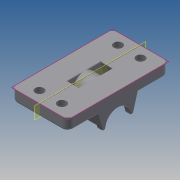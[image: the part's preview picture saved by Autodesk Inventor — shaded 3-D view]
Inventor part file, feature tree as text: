
AUTODESK INVENTOR PART (.ipt)
format: ipt  version: 2014 (Build 180170000, 170)  size: 468,480 bytes
history: native  units: in
note: dims shown in document units (in); Inventor stores cm internally (conversion verified against a paired STEP export)
features: fillet x9, extrude x7, sketch x7, plane x1, mirror x1
ambient origin geometry x8: Origin, YZ Plane, XZ Plane, XY Plane, X Axis, Y Axis, Z Axis, Center Point
bodies: Body1 (feature_tree)
feature tree (25):
  extrude  "Extrusion12"  Depth=1.0441in
  sketch  "Sketch13"  dims[d0=1.1713in d1=1.0441in]
  plane  "Work Plane2"
  extrude  "Extrusion14"  Depth=2.3622in
  extrude  "Extrusion15"  Depth=0.9843in
  mirror  "Mirror2"
  extrude  "Extrusion16"  Depth=0.9449in
  extrude  "Extrusion17"  Depth=0.2362in TaperAngle=0.0deg
  extrude  "Extrusion18"  Depth=0.3346in
  extrude  "Extrusion19"  Depth=0.0197in TaperAngle=0.0deg
  fillet  "Fillet11"  Radius=0.0591in
  fillet  "Fillet12"  Radius=0.1181in
  fillet  "Fillet13"  Radius=0.0394in
  fillet  "Fillet14"  Radius=0.1181in
  fillet  "Fillet15"  Radius=0.1575in
  fillet  "Fillet16"  Radius=0.1575in
  fillet  "Fillet17"  Radius=0.2362in
  fillet  "Fillet18"  Radius=0.4724in
  fillet  "Fillet19"  Radius=0.1811in
  sketch  "Sketch14"  dims[d2=1.5748in d5=2.3622in]
  sketch  "Sketch15"  dims[d6=0.1969in d7=0.9843in]
  sketch  "Sketch16"  dims[d64=0.3543in d65=0.9449in]
  sketch  "Sketch17"  dims[d66=1.7717in d70=0.2362in d71=0.0in]
  sketch  "Sketch18"  dims[d76=0.6299in d77=0.3346in]
  sketch  "Sketch19"  dims[d78=0.1181in d79=1.1811in d80=0.0in d81=0.0591in d82=0.1181in d83=0.0in d84=0.0394in d85=0.1181in d86=0.0in d87=0.1575in d88=0.1575in d89=0.2362in d90=0.0in d91=0.4724in d92=0.1811in d93=1.6535in d94=0.4724in d95=0.2362in d96=0.0in d106=0.0197in d107=0.0197in d108=0.0197in d109=0.0197in d110=0.0197in d111=1.1811in d112=2.126in d113=0.0in d114=0.1181in d115=0.0394in d116=0.2854in d117=0.1181in d118=0.0in d119=0.0197in d120=0.0197in]
